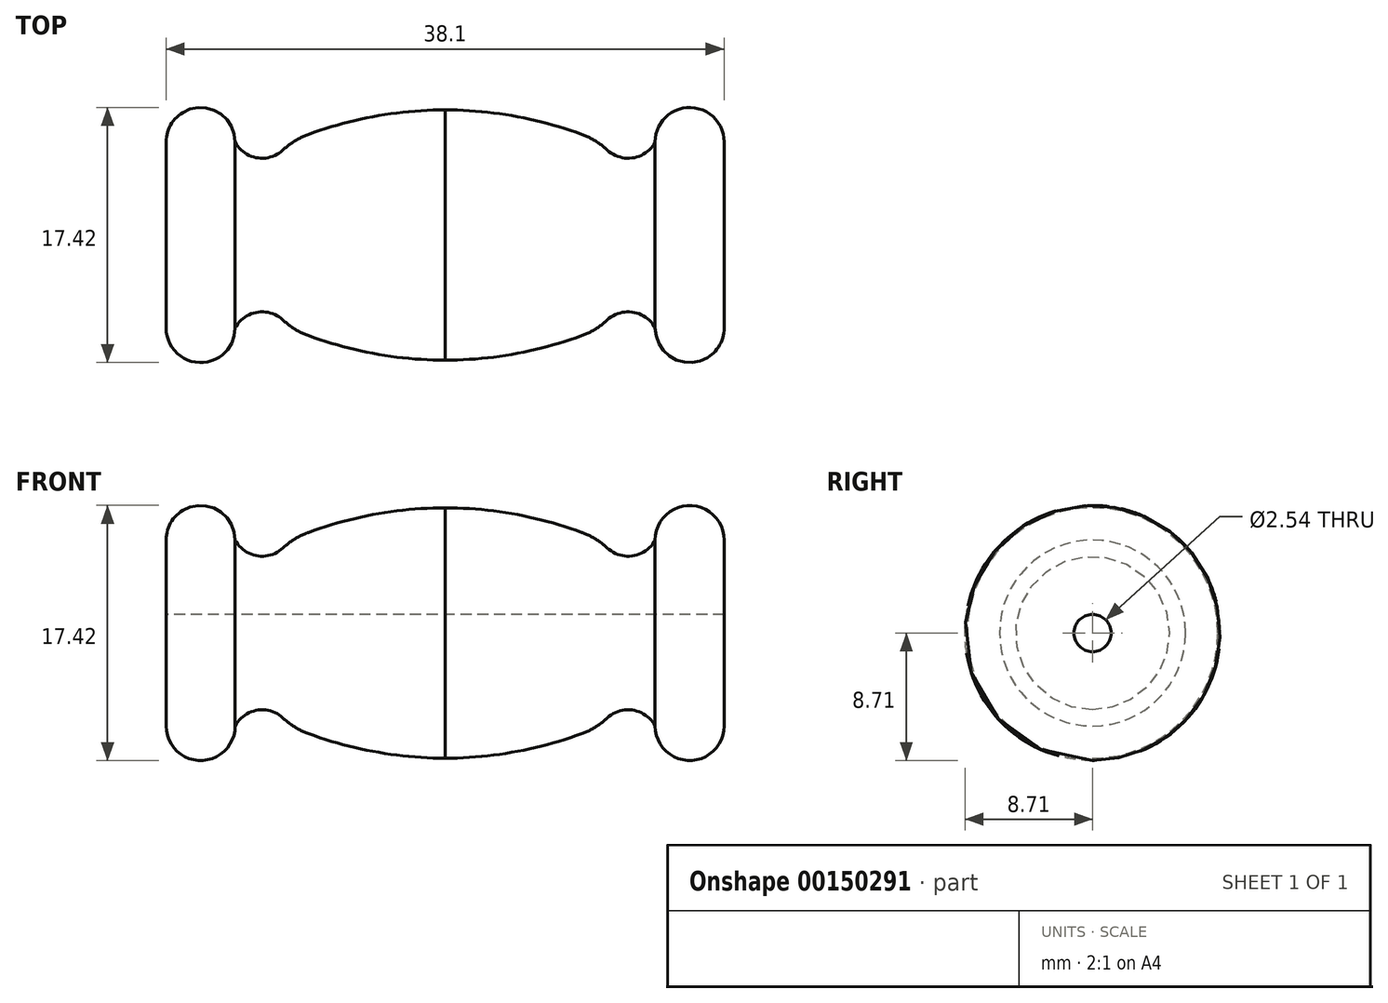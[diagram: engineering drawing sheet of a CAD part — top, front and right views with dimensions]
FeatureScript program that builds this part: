
annotation { "Feature Type Name" : "Feature", "Feature Type Description" : "" }
export const myFeature = defineFeature(function(context is Context, id is Id, definition is map)
    precondition{}
    {
        {
            var Q0;
            Q0=qCreatedBy(makeId("Front.planeOp"),FACE);
            var sketch = newSketch(context, id + "F0", { "sketchPlane" : qUnion([Q0])});
            skLineSegment(sketch, "E0", {"start": v(-19.05, 0) * mm, "end": v(19.05, 0) * mm});
            skLineSegment(sketch, "E1", {"start": v(-19.05, 6.35) * mm, "end": v(-19.05, -6.35) * mm});
            skArc(sketch, "E2", {"start": v(-14.34, 6.35) * mm, "mid": v(-16.7, 8.7) * mm, "end": v(-19.05, 6.35) * mm});
            skArc(sketch, "E3", {"start": v(-14.34, 6.35) * mm, "mid": v(-12.5, 5.24) * mm, "end": v(-10.65, 6.35) * mm});
            skArc(sketch, "E4", {"start": v(10.94, 6.35) * mm, "mid": v(0.15, 8.55) * mm, "end": v(-10.65, 6.35) * mm});
            skLineSegment(sketch, "E5", {"start": v(0, 8.55) * mm, "end": v(0, 0) * mm});
            skLineSegment(sketch, "E6", {"start": v(0, 0) * mm, "end": v(-19.05, 0) * mm});
            skSolve(sketch);
        }
        {
            var Q0;
            {var subQ3=sQuery(id+"F0.wireOp",EDGE,"E2");Q0=makeQuery(id+"F0.imprint","IMPRINT",FACE,{"disambiguationData":[TD([[makeQuery(id+"F0.imprint","IMPRINT",EDGE,{"derivedFrom":subQ3}),1.0]])]});}
            var Q1;
            Q1=sQuery(id+"F0.wireOp",EDGE,"E6");
            revolve(context, id + "F1", {"entities" : qUnion([Q0]), "axis" : qUnion([Q1]), "revolveType" : RevolveType.FULL});
        }
        {
            var Q0;
            Q0=makeQuery(id+"F1.opRevolve","SWEPT_EDGE",EDGE,{"disambiguationData":[OSD([sQuery(id+"F0.wireOp",EDGE,"E3"),sQuery(id+"F0.wireOp",EDGE,"E4")])]});
            fillet(context, id + "F2", {"entities" : qUnion([Q0]), "radius" : 5.08 * mm, "tangentPropagation" : true, "allowEdgeOverflow" : false});
        }
        {
            var Q0;
            Q0=makeQuery(id+"F1.opRevolve","SWEPT_BODY",BODY,{"disambiguationData":[OSD([sQuery(id+"F0.wireOp",EDGE,"E1"),sQuery(id+"F0.wireOp",EDGE,"E2"),sQuery(id+"F0.wireOp",EDGE,"E3"),sQuery(id+"F0.wireOp",EDGE,"E4"),sQuery(id+"F0.wireOp",EDGE,"E5"),sQuery(id+"F0.wireOp",EDGE,"E6")])]});
            var Q1;
            Q1=qCreatedBy(makeId("Right.planeOp"),FACE);
            mirror(context, id + "F3", {"operationType" : NewBodyOperationType.ADD, "entities" : qUnion([Q0]), "mirrorPlane" : qUnion([Q1])});
        }
        {
            var Q0;
            Q0=makeQuery(id+"F1.opRevolve","SWEPT_FACE",FACE,{"disambiguationData":[OSD([sQuery(id+"F0.wireOp",EDGE,"E1")])]});
            var sketch = newSketch(context, id + "F4", { "sketchPlane" : qUnion([Q0])});
            skCircle(sketch, "E7", {"center": v(0, 0) * mm, "radius": 1.27 * mm});
            skSolve(sketch);
        }
        {
            var Q0;
            Q0=makeQuery(id+"F4.imprint","IMPRINT",FACE,{"disambiguationData":[TD([[makeQuery(id+"F4.imprint","IMPRINT",EDGE,{"derivedFrom":sQuery(id+"F4.wireOp",EDGE,"E7")}),1.0]])]});
            extrude(context, id + "F5", {"entities" : qUnion([Q0]), "operationType" : NewBodyOperationType.REMOVE, "endBound" : BoundingType.THROUGH_ALL, "oppositeDirection" : true, "depth" : 25.4 * mm});
        }
    });
